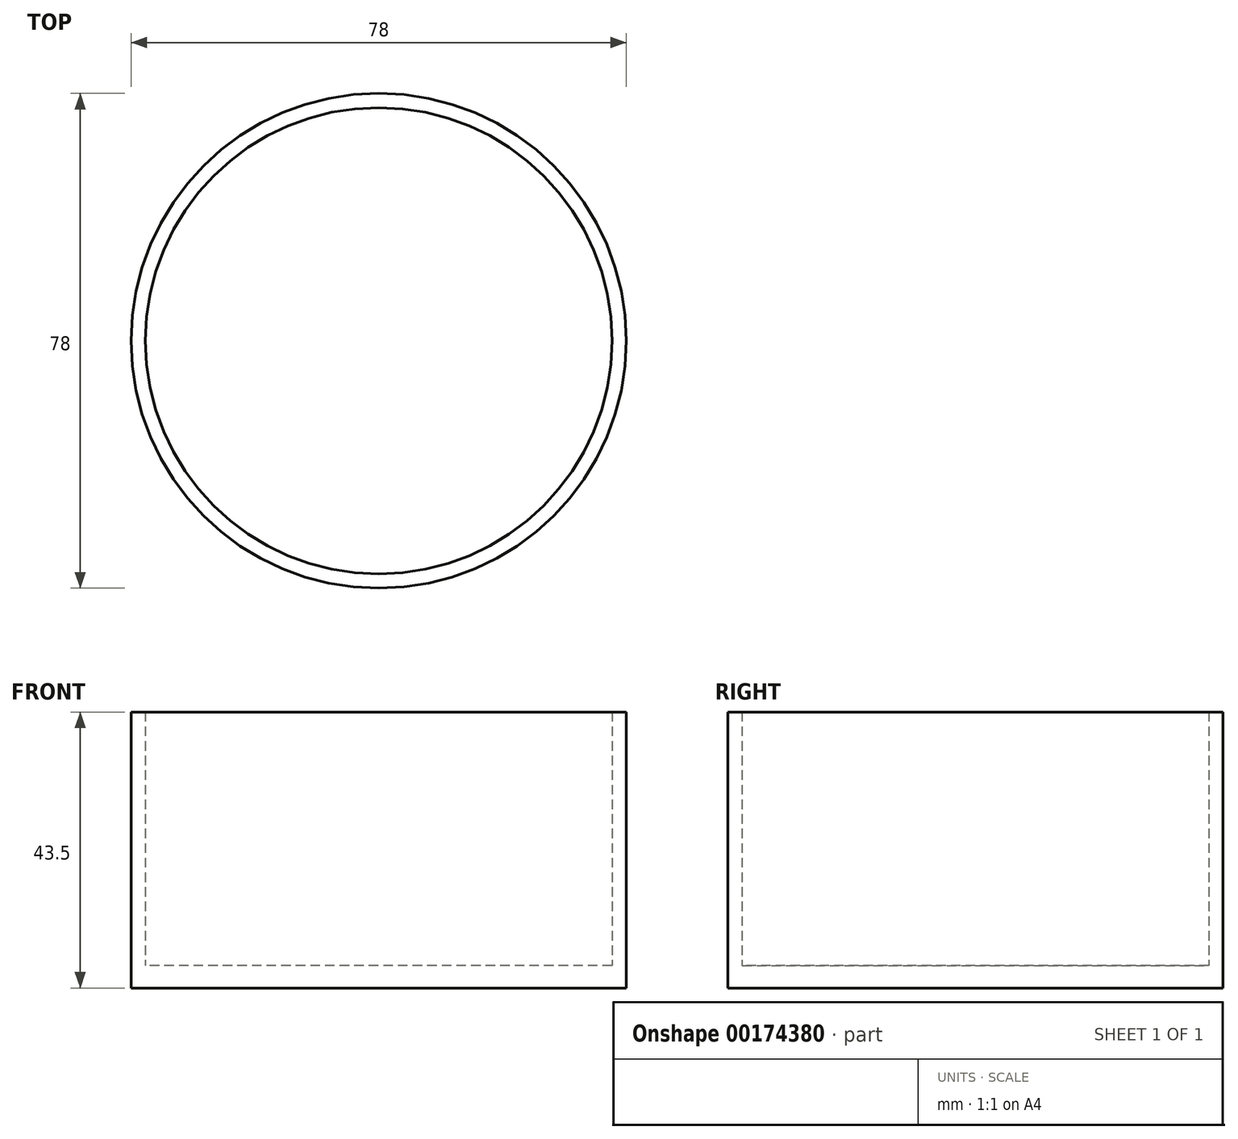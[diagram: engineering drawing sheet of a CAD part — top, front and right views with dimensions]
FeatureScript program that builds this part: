
annotation { "Feature Type Name" : "Feature", "Feature Type Description" : "" }
export const myFeature = defineFeature(function(context is Context, id is Id, definition is map)
    precondition{}
    {
        {
            var Q0;
            Q0=qCreatedBy(makeId("Top.planeOp"),FACE);
            var sketch = newSketch(context, id + "F0", { "sketchPlane" : qUnion([Q0])});
            skCircle(sketch, "E0", {"center": v(0, 0) * mm, "radius": 39 * mm});
            skSolve(sketch);
        }
        {
            var Q0;
            Q0=makeQuery(id+"F0.imprint","IMPRINT",FACE,{"disambiguationData":[TD([[makeQuery(id+"F0.imprint","IMPRINT",EDGE,{"derivedFrom":sQuery(id+"F0.wireOp",EDGE,"E0")}),1.0]])]});
            extrude(context, id + "F1", {"entities" : qUnion([Q0]), "depth" : 1.5 * mm});
        }
        {
            var Q0;
            Q0=makeQuery(id+"F1.opExtrude","CAP_FACE",FACE,{"disambiguationData":[OSD([sQuery(id+"F0.wireOp",EDGE,"E0")])],"isStart":false});
            var sketch = newSketch(context, id + "F2", { "sketchPlane" : qUnion([Q0])});
            skCircle(sketch, "E1", {"center": v(0, 0) * mm, "radius": 39 * mm});
            skCircle(sketch, "E2.0", {"center": v(0, 0) * mm, "radius": 36.75 * mm});
            skSolve(sketch);
        }
        {
            var Q0;
            Q0 = qSketchRegion(id + "F2", true);
            extrude(context, id + "F3", {"entities" : qUnion([Q0]), "operationType" : NewBodyOperationType.ADD, "depth" : 40 * mm});
        }
        {
            var Q0;
            Q0=makeQuery(id+"F1.opExtrude","CAP_FACE",FACE,{"disambiguationData":[OSD([sQuery(id+"F0.wireOp",EDGE,"E0")])],"isStart":true});
            extrude(context, id + "F4", {"entities" : qUnion([Q0]), "operationType" : NewBodyOperationType.ADD, "depth" : 2 * mm});
        }
    });
